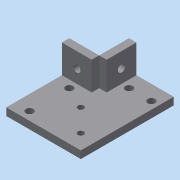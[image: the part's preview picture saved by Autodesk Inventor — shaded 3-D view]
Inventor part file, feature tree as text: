
AUTODESK INVENTOR PART (.ipt)
format: ipt  version: 2015 (Build 190159000, 159)  size: 144,896 bytes
history: native  units: mm
features: sketch x6, hole x6, extrude x3
ambient origin geometry x8: Origin, YZ Plane, XZ Plane, XY Plane, X Axis, Y Axis, Z Axis, Center Point
bodies: Solid1 (feature_tree)
feature tree (15):
  sketch  "Sketch1"  dims[d0=30.0mm d16=42.3mm]
  extrude  "Extrusion1"  Depth=42.3mm
  hole  "Hole2"  [1 undecoded]
  extrude  "Extrusion2"  Depth=5.0mm TaperAngle=0.0deg
  hole  "Hole3"  [1 undecoded]
  hole  "Hole4"  [1 undecoded]
  hole  "Hole5"  [1 undecoded]
  extrude  "Extrusion3"  Depth=25.0mm
  hole  "Hole6"  [1 undecoded]
  hole  "Hole7"  [1 undecoded]
  sketch  "Sketch2"  dims[d21=20.0mm d22=20.0mm]
  sketch  "Sketch3"  dims[d23=5.0mm d24=0.0mm]
  sketch  "Sketch4"  dims[d32=5.0mm d33=6.0mm d34=4.0mm d35=2.0mm d36=90.0deg d37=8.0mm d38=20.594885mm d40=5.0mm d41=0.0mm]
  sketch  "Sketch5"  dims[d42=5.0mm d43=6.0mm d44=4.0mm d45=2.0mm d46=90.0deg d47=8.0mm d48=20.594885mm d49=30.0mm]
  sketch  "Sketch6"  dims[d50=5.0mm d51=10.0mm d52=10.0mm d53=4.0mm d54=6.0mm d55=4.0mm d56=2.0mm d57=90.0deg d58=8.0mm d59=20.594885mm d60=25.0mm d61=25.0mm d62=4.0mm d63=6.0mm d64=4.0mm d65=2.0mm d66=90.0deg d67=8.0mm d68=20.594885mm d69=10.0mm d70=10.0mm d71=10.0mm d72=5.0mm d73=5.0mm d74=19.0mm d75=0.0mm d76=10.0mm d77=10.0mm d78=5.0mm d79=6.0mm d80=4.0mm d81=2.0mm d82=90.0deg d83=8.0mm d84=20.594885mm d85=10.0mm d86=10.0mm d87=5.0mm d88=6.0mm d89=4.0mm d90=2.0mm d91=90.0deg d92=8.0mm d93=20.594885mm]
note: 6 required parameter values undecoded (feature->parameter linkage not recoverable at this tier; creation-order binding heuristic only, values carry confidence <= 0.55)
